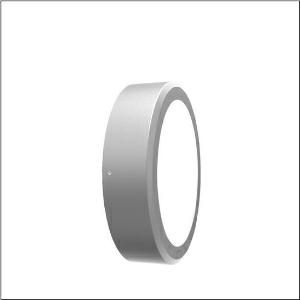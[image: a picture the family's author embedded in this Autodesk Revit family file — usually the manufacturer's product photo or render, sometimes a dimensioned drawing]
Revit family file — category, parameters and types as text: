
# Revit family: cl_31_bulkhead_5cl721603
name_source: partatom
category: Lighting Fixtures
units: mm (PartAtom-declared; Revit-internal decimal feet)

## family parameters
Cut with Voids When Loaded = No
Host = Face
Light Source = No
Part Type = Normal
Room Calculation Point = No
Round Connector Dimension = Use Diameter
Shared = No

## types (1)
- --- (1 x LED, 1570 lm, 14.9 W, 3000K)
    Apparent Load = 15 VA
    CIE Flux Codes = 46 78 95 100 100
    Color Rendering = 80
    Color Temperature = 3000K
    Default Elevation = 1800 mm
    Description = CL 31 Bulkhead, wall and ceiling luminaire, primary light control with reflector, primary optical cover: cover panel, of PC, opal, primary light characteristic: symmetric, installation type: surface-mounted, LED, rated luminous flux: 1.575lm, luminous efficacy: 105lm/W, light colour: 830, colour temperature: 3000K, control gear: ECG DALI, with terminal, 5-pole, max. 2.5mm², mains connection: 220..240V, AC, 50/60Hz, rated input power: 15W, luminaire housing, round, of aluminium, powder-coated, Siteco® metallic grey, diameter: 264mm, height: 63mm, protection rating (complete): IP65, insulation class (complete): insulation class I (protective earthing), certification: CE, ENEC, impact resistance: IK09, permissible operating ambient temperature for outdoor applications: -20..+50°C, packaging unit: 1 piece
    Height = 63 mm
    Lamp = 1 x LED
    Lamp Light Flux = 1570 lm
    Lamp Power = 14.9 W
    Lamp count = 1
    Length = 264 mm
    Luminous efficacy = 105 lm/W
    Manufacturer = Siteco
    ModVariant = No
    Model = 5CL721603
    Mounting Place = Ceiling
    Mounting Type = Surface mounted
    Number of Poles = 1
    OnlyDefault = Yes
    Power Factor = 1
    Product Name = CL 31 Bulkhead
    Product group = wall and ceiling luminaire
    ProductGroupID = 301
    Protection Class = Protection class I
    Protection Degree = IP 65
    RLX_Detail_Level = 1
    RLX_Emergency_Light_Flux = 0 lm
    RLX_Emergency_Type = 0
    RLX_Emergency_Type_DB = No
    RlxData = <blob elided: 36541 chars, md5=e647e4c8>
    Socket = socket
    Standby Power = 0 W
    System Light Flux = 1570 lm
    System Power = 15 W
    Type Comments = factory setting: luminous flux: 100 % | dim-lin: 254 | 347 mA
    Type Image = l_1006885.jpg
    URL = http://relux.com
    VarID = @adj_130479
    Voltage = 0 V
    Weight = 0.00 kg
    Width = 0 mm  [stored 0 ft]

note: [stored X ft] marks values corroborated as IEEE doubles in the binary element streams (Revit-internal decimal feet)

## geometry (parser evidence)
native form markers: Blend x4, Sweep x11
no freeform markers — native parametric forms only
